# Revit family: Detectable-Warning-Surfaces_Cast-Iron-Dome-Tapered-Wedge-R15-5X24_ADA-Solutions
name_source: partatom
category: Generic Models
units: mm (PartAtom-declared; Revit-internal decimal feet)

## family parameters
Always vertical = Yes
Can host rebar = No
Cut with Voids When Loaded = No
Host = Floor
Maintain Annotation Orientation = No
Part Type = Normal
Room Calculation Point = No
Round Connector Dimension = Use Diameter
Shared = No

## types (9) — shared parameters
Default Elevation = 0"
Keynote = 09 33 00
Length = 5"
Manufacturer = ADA Solutions
Model = Iron Dome Cast Iron
Product Page URL = https://www.arcat.com
URL = https://adatile.com
Width = 24"

## type names (no varying parameters)
- ADA Dark Gray
- ADA Black
- ADA Blue
- ADA Yellow
- ADA Seattle Yellow
- ADA Safety Red
- ADA White
- ADA Clay Red
- ADA Brick Red

note: column(s) folded — value = type name in every type: Color

## geometry (parser evidence)
native form markers: Sweep x2
no freeform markers — native parametric forms only
